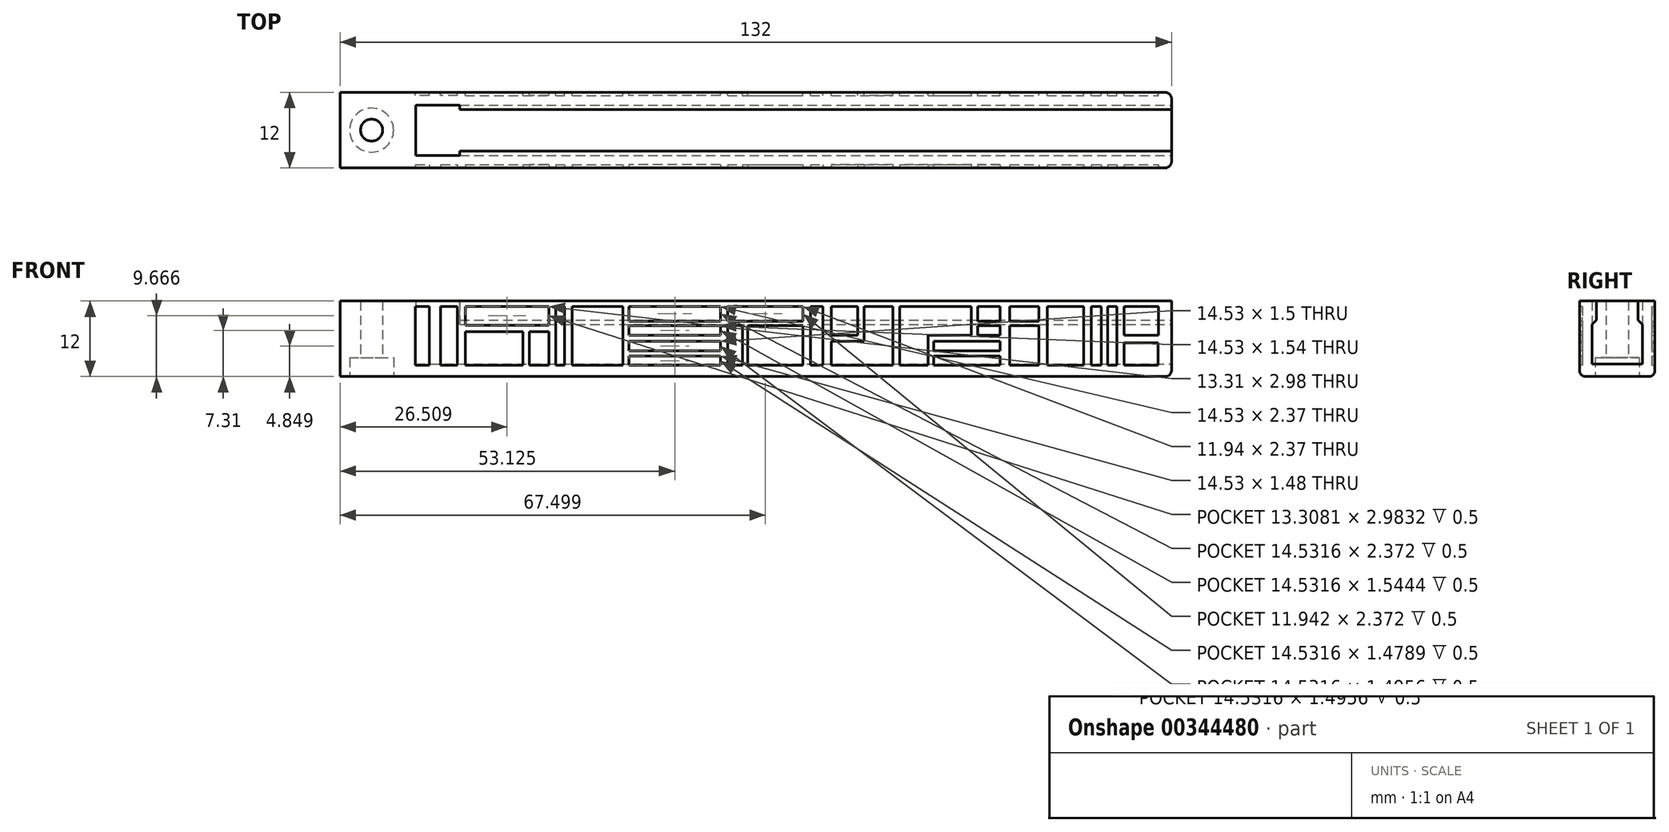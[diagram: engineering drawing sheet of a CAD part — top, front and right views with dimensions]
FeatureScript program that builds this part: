
annotation { "Feature Type Name" : "Feature", "Feature Type Description" : "" }
export const myFeature = defineFeature(function(context is Context, id is Id, definition is map)
    precondition{}
    {
        {
            var Q0;
            Q0=qCreatedBy(makeId("Top.planeOp"),FACE);
            var sketch = newSketch(context, id + "F0", { "sketchPlane" : qUnion([Q0])});
            skLineSegment(sketch, "E0.bottom", {"start": v(0, 0) * mm, "end": v(132, 0) * mm});
            skLineSegment(sketch, "E0.top", {"start": v(0, 12) * mm, "end": v(132, 12) * mm});
            skLineSegment(sketch, "E0.left", {"start": v(0, 0) * mm, "end": v(0, 12) * mm});
            skLineSegment(sketch, "E0.right", {"start": v(132, 0) * mm, "end": v(132, 12) * mm});
            skSolve(sketch);
        }
        {
            var Q0;
            Q0 = qSketchRegion(id + "F0", true);
            extrude(context, id + "F1", {"entities" : qUnion([Q0]), "depth" : 12 * mm, "offsetDistance" : 25 * mm});
        }
        {
            var Q0;
            Q0=makeQuery(id+"F1.opExtrude","SWEPT_FACE",FACE,{"disambiguationData":[OSD([sQuery(id+"F0.wireOp",EDGE,"E0.right")])]});
            var sketch = newSketch(context, id + "F2", { "sketchPlane" : qUnion([Q0])});
            skLineSegment(sketch, "E1.MirrorCS", {"start": v(2.7, 12) * mm, "end": v(2.7, 9) * mm});
            skLineSegment(sketch, "E2.MirrorCS", {"start": v(2.7, 9) * mm, "end": v(2, 8.3) * mm});
            skLineSegment(sketch, "E3.MirrorCS", {"start": v(2, 8.3) * mm, "end": v(2, 2) * mm});
            skLineSegment(sketch, "E4.MirrorCS", {"start": v(2, 2) * mm, "end": v(6, 2) * mm});
            skLineSegment(sketch, "E5", {"start": v(6, 2) * mm, "end": v(6, 12.64) * mm, "construction": true});
            skLineSegment(sketch, "E6.MirrorCS", {"start": v(9.3, 12) * mm, "end": v(9.3, 9) * mm});
            skLineSegment(sketch, "E7.MirrorCS", {"start": v(9.3, 9) * mm, "end": v(10, 8.3) * mm});
            skLineSegment(sketch, "E8.MirrorCS", {"start": v(10, 8.3) * mm, "end": v(10, 2) * mm});
            skLineSegment(sketch, "E9.MirrorCS", {"start": v(10, 2) * mm, "end": v(6, 2) * mm});
            skSolve(sketch);
        }
        {
            var Q0;
            {var subQ0=sQuery(id+"F2.wireOp",EDGE,"E1.MirrorCS");Q0=makeQuery(id+"F2.imprint","IMPRINT",FACE,{"disambiguationData":[TD([[makeQuery(id+"F2.imprint","IMPRINT",EDGE,{"derivedFrom":subQ0}),1.0]])]});}
            extrude(context, id + "F3", {"entities" : qUnion([Q0]), "operationType" : NewBodyOperationType.REMOVE, "oppositeDirection" : true, "depth" : 120 * mm, "offsetDistance" : 25 * mm});
        }
        {
            var Q0;
            Q0=makeQuery(id+"F1.opExtrude","CAP_EDGE",EDGE,{"disambiguationData":[OSD([sQuery(id+"F0.wireOp",EDGE,"E0.top")])],"isStart":true});
            var Q1;
            Q1=makeQuery(id+"F1.opExtrude","CAP_EDGE",EDGE,{"disambiguationData":[OSD([sQuery(id+"F0.wireOp",EDGE,"E0.bottom")])],"isStart":true});
            fillet(context, id + "F4", {"entities" : qUnion([Q0, Q1]), "radius" : 1 * mm, "tangentPropagation" : true, "allowEdgeOverflow" : false});
        }
        {
            var Q0;
            Q0=makeQuery(id+"F1.opExtrude","SWEPT_EDGE",EDGE,{"disambiguationData":[OSD([sQuery(id+"F0.wireOp",EDGE,"E0.top"),sQuery(id+"F0.wireOp",EDGE,"E0.right")])]});
            fillet(context, id + "F5", {"entities" : qUnion([Q0]), "radius" : 1 * mm, "tangentPropagation" : true, "allowEdgeOverflow" : false});
        }
        {
            var Q0;
            Q0=makeQuery(id+"F1.opExtrude","CAP_FACE",FACE,{"disambiguationData":[OSD([sQuery(id+"F0.wireOp",EDGE,"E0.bottom"),sQuery(id+"F0.wireOp",EDGE,"E0.top"),sQuery(id+"F0.wireOp",EDGE,"E0.left"),sQuery(id+"F0.wireOp",EDGE,"E0.right")])],"isStart":true});
            var sketch = newSketch(context, id + "F6", { "sketchPlane" : qUnion([Q0])});
            skCircle(sketch, "E10", {"center": v(5, -6) * mm, "radius": 1.75 * mm});
            skPoint(sketch, "E10.centerSnap0", {"position": v(0, -6) * mm});
            skSolve(sketch);
        }
        {
            var Q0;
            Q0 = qSketchRegion(id + "F6", true);
            extrude(context, id + "F7", {"entities" : qUnion([Q0]), "operationType" : NewBodyOperationType.REMOVE, "oppositeDirection" : true, "depth" : 25 * mm, "offsetDistance" : 25 * mm});
        }
        {
            var Q0;
            Q0=makeQuery(id+"F1.opExtrude","CAP_FACE",FACE,{"disambiguationData":[OSD([sQuery(id+"F0.wireOp",EDGE,"E0.bottom"),sQuery(id+"F0.wireOp",EDGE,"E0.top"),sQuery(id+"F0.wireOp",EDGE,"E0.left"),sQuery(id+"F0.wireOp",EDGE,"E0.right")])],"isStart":true});
            var sketch = newSketch(context, id + "F8", { "sketchPlane" : qUnion([Q0])});
            skCircle(sketch, "E11", {"center": v(5, -6) * mm, "radius": 3.5 * mm});
            skSolve(sketch);
        }
        {
            var Q0;
            Q0 = qSketchRegion(id + "F8", true);
            extrude(context, id + "F9", {"entities" : qUnion([Q0]), "operationType" : NewBodyOperationType.REMOVE, "oppositeDirection" : true, "depth" : 3 * mm, "offsetDistance" : 25 * mm});
        }
        {
            var Q0;
            Q0=makeQuery(id+"F3.boolean.opBoolean","COPY",FACE,{"derivedFrom":makeQuery(id+"F3.opExtrude","SWEPT_FACE",FACE,{"disambiguationData":[OSD([sQuery(id+"F2.wireOp",EDGE,"E4.MirrorCS"),sQuery(id+"F2.wireOp",EDGE,"E9.MirrorCS")])]})});
            var sketch = newSketch(context, id + "F10", { "sketchPlane" : qUnion([Q0])});
            skLineSegment(sketch, "E12.bottom", {"start": v(12, 10) * mm, "end": v(19, 10) * mm});
            skLineSegment(sketch, "E12.top", {"start": v(12, 2) * mm, "end": v(19, 2) * mm});
            skLineSegment(sketch, "E12.left", {"start": v(12, 10) * mm, "end": v(12, 2) * mm});
            skLineSegment(sketch, "E12.right", {"start": v(19, 10) * mm, "end": v(19, 2) * mm});
            skSolve(sketch);
        }
        {
            var Q0;
            Q0 = qSketchRegion(id + "F10", true);
            extrude(context, id + "F11", {"entities" : qUnion([Q0]), "operationType" : NewBodyOperationType.REMOVE, "depth" : 25 * mm, "offsetDistance" : 25 * mm});
        }
        {
            var Q0;
            Q0=makeQuery(id+"F1.opExtrude","SWEPT_FACE",FACE,{"disambiguationData":[OSD([sQuery(id+"F0.wireOp",EDGE,"E0.top")])]});
            var sketch = newSketch(context, id + "F12", { "sketchPlane" : qUnion([Q0])});
            skLineSegment(sketch, "E13.bottom", {"start": v(-19.85, 1.79) * mm, "end": v(-19.85, 7.11) * mm});
            skLineSegment(sketch, "E13.top", {"start": v(-29.03, 1.79) * mm, "end": v(-29.03, 7.11) * mm});
            skLineSegment(sketch, "E13.left", {"start": v(-19.85, 1.79) * mm, "end": v(-29.03, 1.79) * mm});
            skLineSegment(sketch, "E13.right", {"start": v(-19.85, 7.11) * mm, "end": v(-29.03, 7.11) * mm});
            skLineSegment(sketch, "E14.bottom", {"start": v(-19.85, 8.17) * mm, "end": v(-19.85, 11.16) * mm});
            skLineSegment(sketch, "E14.top", {"start": v(-33.16, 8.17) * mm, "end": v(-33.16, 11.16) * mm});
            skLineSegment(sketch, "E14.left", {"start": v(-19.85, 8.17) * mm, "end": v(-33.16, 8.17) * mm});
            skLineSegment(sketch, "E14.right", {"start": v(-19.85, 11.16) * mm, "end": v(-33.16, 11.16) * mm});
            skPoint(sketch, "E15.firstSnap0", {"position": v(-33.16, 9.67) * mm});
            skLineSegment(sketch, "E15.bottom", {"start": v(-33.16, 1.79) * mm, "end": v(-33.16, 7.11) * mm});
            skLineSegment(sketch, "E15.top", {"start": v(-30.04, 1.79) * mm, "end": v(-30.04, 7.11) * mm});
            skLineSegment(sketch, "E15.left", {"start": v(-33.16, 1.79) * mm, "end": v(-30.04, 1.79) * mm});
            skLineSegment(sketch, "E15.right", {"start": v(-33.16, 7.11) * mm, "end": v(-30.04, 7.11) * mm});
            skLineSegment(sketch, "E16.bottom", {"start": v(-34.2, 1.79) * mm, "end": v(-34.2, 11.16) * mm});
            skLineSegment(sketch, "E16.top", {"start": v(-35.66, 1.79) * mm, "end": v(-35.66, 11.16) * mm});
            skLineSegment(sketch, "E16.left", {"start": v(-34.2, 1.79) * mm, "end": v(-35.66, 1.79) * mm});
            skLineSegment(sketch, "E16.right", {"start": v(-34.2, 11.16) * mm, "end": v(-35.66, 11.16) * mm});
            skLineSegment(sketch, "E17.bottom", {"start": v(-36.83, 1.79) * mm, "end": v(-36.83, 11.16) * mm});
            skLineSegment(sketch, "E17.top", {"start": v(-44.9, 1.79) * mm, "end": v(-44.9, 11.16) * mm});
            skLineSegment(sketch, "E17.left", {"start": v(-36.83, 1.79) * mm, "end": v(-44.9, 1.79) * mm});
            skLineSegment(sketch, "E17.right", {"start": v(-36.83, 11.16) * mm, "end": v(-44.9, 11.16) * mm});
            skLineSegment(sketch, "E18.bottom", {"start": v(-45.86, 1.79) * mm, "end": v(-45.86, 3.27) * mm});
            skLineSegment(sketch, "E18.top", {"start": v(-60.4, 1.79) * mm, "end": v(-60.4, 3.27) * mm});
            skLineSegment(sketch, "E18.left", {"start": v(-45.86, 1.79) * mm, "end": v(-60.4, 1.79) * mm});
            skLineSegment(sketch, "E18.right", {"start": v(-45.86, 3.27) * mm, "end": v(-60.4, 3.27) * mm});
            skLineSegment(sketch, "E19.bottom", {"start": v(-60.4, 4.1) * mm, "end": v(-60.4, 5.6) * mm});
            skLineSegment(sketch, "E19.top", {"start": v(-45.86, 4.1) * mm, "end": v(-45.86, 5.6) * mm});
            skLineSegment(sketch, "E19.left", {"start": v(-60.4, 4.1) * mm, "end": v(-45.86, 4.1) * mm});
            skLineSegment(sketch, "E19.right", {"start": v(-60.4, 5.6) * mm, "end": v(-45.86, 5.6) * mm});
            skLineSegment(sketch, "E20.bottom", {"start": v(-45.86, 6.54) * mm, "end": v(-45.86, 8.08) * mm});
            skLineSegment(sketch, "E20.top", {"start": v(-60.4, 6.54) * mm, "end": v(-60.4, 8.08) * mm});
            skLineSegment(sketch, "E20.left", {"start": v(-45.86, 6.54) * mm, "end": v(-60.4, 6.54) * mm});
            skLineSegment(sketch, "E20.right", {"start": v(-45.86, 8.08) * mm, "end": v(-60.4, 8.08) * mm});
            skLineSegment(sketch, "E21.bottom", {"start": v(-60.4, 8.79) * mm, "end": v(-60.4, 11.16) * mm});
            skLineSegment(sketch, "E21.top", {"start": v(-45.86, 8.79) * mm, "end": v(-45.86, 11.16) * mm});
            skLineSegment(sketch, "E21.left", {"start": v(-60.4, 8.79) * mm, "end": v(-45.86, 8.79) * mm});
            skLineSegment(sketch, "E21.right", {"start": v(-60.4, 11.16) * mm, "end": v(-45.86, 11.16) * mm});
            skLineSegment(sketch, "E22.bottom", {"start": v(-61.53, 1.79) * mm, "end": v(-61.53, 8.08) * mm});
            skLineSegment(sketch, "E22.top", {"start": v(-63.86, 1.79) * mm, "end": v(-63.86, 8.08) * mm});
            skLineSegment(sketch, "E22.left", {"start": v(-61.53, 1.79) * mm, "end": v(-63.86, 1.79) * mm});
            skLineSegment(sketch, "E22.right", {"start": v(-61.53, 8.08) * mm, "end": v(-63.86, 8.08) * mm});
            skLineSegment(sketch, "E23.bottom", {"start": v(-61.53, 8.79) * mm, "end": v(-61.53, 11.16) * mm});
            skLineSegment(sketch, "E23.top", {"start": v(-73.47, 8.79) * mm, "end": v(-73.47, 11.16) * mm});
            skLineSegment(sketch, "E23.left", {"start": v(-61.53, 8.79) * mm, "end": v(-73.47, 8.79) * mm});
            skLineSegment(sketch, "E23.right", {"start": v(-61.53, 11.16) * mm, "end": v(-73.47, 11.16) * mm});
            skLineSegment(sketch, "E24.bottom", {"start": v(-64.7, 1.79) * mm, "end": v(-64.7, 8.08) * mm});
            skLineSegment(sketch, "E24.top", {"start": v(-73.47, 1.79) * mm, "end": v(-73.47, 8.08) * mm});
            skLineSegment(sketch, "E24.left", {"start": v(-64.7, 1.79) * mm, "end": v(-73.47, 1.79) * mm});
            skLineSegment(sketch, "E24.right", {"start": v(-64.7, 8.08) * mm, "end": v(-73.47, 8.08) * mm});
            skLineSegment(sketch, "E25.bottom", {"start": v(-74.65, 11.16) * mm, "end": v(-74.65, 1.79) * mm});
            skLineSegment(sketch, "E25.top", {"start": v(-76.62, 11.16) * mm, "end": v(-76.62, 1.79) * mm});
            skLineSegment(sketch, "E25.left", {"start": v(-74.65, 11.16) * mm, "end": v(-76.62, 11.16) * mm});
            skLineSegment(sketch, "E25.right", {"start": v(-74.65, 1.79) * mm, "end": v(-76.62, 1.79) * mm});
            skLineSegment(sketch, "E26.bottom", {"start": v(-77.98, 11.16) * mm, "end": v(-77.98, 6.54) * mm});
            skLineSegment(sketch, "E26.top", {"start": v(-82.17, 11.16) * mm, "end": v(-82.17, 6.54) * mm});
            skLineSegment(sketch, "E26.left", {"start": v(-77.98, 11.16) * mm, "end": v(-82.17, 11.16) * mm});
            skLineSegment(sketch, "E26.right", {"start": v(-77.98, 6.54) * mm, "end": v(-82.17, 6.54) * mm});
            skLineSegment(sketch, "E27.bottom", {"start": v(-77.98, 5.6) * mm, "end": v(-77.98, 1.79) * mm});
            skLineSegment(sketch, "E27.top", {"start": v(-87.79, 5.6) * mm, "end": v(-87.79, 1.79) * mm});
            skLineSegment(sketch, "E27.left", {"start": v(-77.98, 5.6) * mm, "end": v(-87.79, 5.6) * mm});
            skLineSegment(sketch, "E27.right", {"start": v(-77.98, 1.79) * mm, "end": v(-87.79, 1.79) * mm});
            skLineSegment(sketch, "E28.bottom", {"start": v(-87.79, 5.6) * mm, "end": v(-87.79, 11.16) * mm});
            skLineSegment(sketch, "E28.top", {"start": v(-83.2, 5.6) * mm, "end": v(-83.2, 11.16) * mm});
            skLineSegment(sketch, "E28.left", {"start": v(-87.79, 5.6) * mm, "end": v(-83.2, 5.6) * mm});
            skLineSegment(sketch, "E28.right", {"start": v(-87.79, 11.16) * mm, "end": v(-83.2, 11.16) * mm});
            skLineSegment(sketch, "E29.bottom", {"start": v(-88.87, 1.79) * mm, "end": v(-88.87, 11.16) * mm});
            skLineSegment(sketch, "E29.top", {"start": v(-93.38, 1.79) * mm, "end": v(-93.38, 11.16) * mm});
            skLineSegment(sketch, "E29.left", {"start": v(-88.87, 1.79) * mm, "end": v(-93.38, 1.79) * mm});
            skLineSegment(sketch, "E29.right", {"start": v(-88.87, 11.16) * mm, "end": v(-93.38, 11.16) * mm});
            skLineSegment(sketch, "E30.bottom", {"start": v(-93.38, 11.16) * mm, "end": v(-93.38, 6.54) * mm});
            skLineSegment(sketch, "E30.top", {"start": v(-100.19, 11.16) * mm, "end": v(-100.19, 6.54) * mm});
            skLineSegment(sketch, "E30.left", {"start": v(-93.38, 11.16) * mm, "end": v(-100.19, 11.16) * mm});
            skLineSegment(sketch, "E30.right", {"start": v(-93.38, 6.54) * mm, "end": v(-100.19, 6.54) * mm});
            skLineSegment(sketch, "E31.bottom", {"start": v(-94.25, 1.79) * mm, "end": v(-94.25, 3.27) * mm});
            skLineSegment(sketch, "E31.top", {"start": v(-104.75, 1.79) * mm, "end": v(-104.75, 3.27) * mm});
            skLineSegment(sketch, "E31.left", {"start": v(-94.25, 1.79) * mm, "end": v(-104.75, 1.79) * mm});
            skLineSegment(sketch, "E31.right", {"start": v(-94.25, 3.27) * mm, "end": v(-104.75, 3.27) * mm});
            skLineSegment(sketch, "E32.bottom", {"start": v(-94.25, 4.1) * mm, "end": v(-94.25, 5.6) * mm});
            skLineSegment(sketch, "E32.top", {"start": v(-104.75, 4.1) * mm, "end": v(-104.75, 5.6) * mm});
            skLineSegment(sketch, "E32.left", {"start": v(-94.25, 4.1) * mm, "end": v(-104.75, 4.1) * mm});
            skLineSegment(sketch, "E32.right", {"start": v(-94.25, 5.6) * mm, "end": v(-104.75, 5.6) * mm});
            skLineSegment(sketch, "E33.bottom", {"start": v(-104.75, 6.54) * mm, "end": v(-104.75, 8.08) * mm});
            skLineSegment(sketch, "E33.top", {"start": v(-101.21, 6.54) * mm, "end": v(-101.21, 8.08) * mm});
            skLineSegment(sketch, "E33.left", {"start": v(-104.75, 6.54) * mm, "end": v(-101.21, 6.54) * mm});
            skLineSegment(sketch, "E33.right", {"start": v(-104.75, 8.08) * mm, "end": v(-101.21, 8.08) * mm});
            skLineSegment(sketch, "E34.bottom", {"start": v(-101.21, 8.79) * mm, "end": v(-101.21, 11.16) * mm});
            skLineSegment(sketch, "E34.top", {"start": v(-104.75, 8.79) * mm, "end": v(-104.75, 11.16) * mm});
            skLineSegment(sketch, "E34.left", {"start": v(-101.21, 8.79) * mm, "end": v(-104.75, 8.79) * mm});
            skLineSegment(sketch, "E34.right", {"start": v(-101.21, 11.16) * mm, "end": v(-104.75, 11.16) * mm});
            skLineSegment(sketch, "E35.bottom", {"start": v(-106.32, 1.79) * mm, "end": v(-106.32, 8.08) * mm});
            skLineSegment(sketch, "E35.top", {"start": v(-110.94, 1.79) * mm, "end": v(-110.94, 8.08) * mm});
            skLineSegment(sketch, "E35.left", {"start": v(-106.32, 1.79) * mm, "end": v(-110.94, 1.79) * mm});
            skLineSegment(sketch, "E35.right", {"start": v(-106.32, 8.08) * mm, "end": v(-110.94, 8.08) * mm});
            skLineSegment(sketch, "E36.bottom", {"start": v(-112.25, 1.79) * mm, "end": v(-112.25, 11.16) * mm});
            skLineSegment(sketch, "E36.top", {"start": v(-118.04, 1.79) * mm, "end": v(-118.04, 11.16) * mm});
            skLineSegment(sketch, "E36.left", {"start": v(-112.25, 1.79) * mm, "end": v(-118.04, 1.79) * mm});
            skLineSegment(sketch, "E36.right", {"start": v(-112.25, 11.16) * mm, "end": v(-118.04, 11.16) * mm});
            skLineSegment(sketch, "E37.bottom", {"start": v(-106.32, 8.79) * mm, "end": v(-106.32, 11.16) * mm});
            skLineSegment(sketch, "E37.top", {"start": v(-110.94, 8.79) * mm, "end": v(-110.94, 11.16) * mm});
            skLineSegment(sketch, "E37.left", {"start": v(-106.32, 8.79) * mm, "end": v(-110.94, 8.79) * mm});
            skLineSegment(sketch, "E37.right", {"start": v(-106.32, 11.16) * mm, "end": v(-110.94, 11.16) * mm});
            skLineSegment(sketch, "E38.bottom", {"start": v(-119.28, 1.79) * mm, "end": v(-119.28, 11.16) * mm});
            skLineSegment(sketch, "E38.top", {"start": v(-120.87, 1.79) * mm, "end": v(-120.87, 11.16) * mm});
            skLineSegment(sketch, "E38.left", {"start": v(-119.28, 1.79) * mm, "end": v(-120.87, 1.79) * mm});
            skLineSegment(sketch, "E38.right", {"start": v(-119.28, 11.16) * mm, "end": v(-120.87, 11.16) * mm});
            skLineSegment(sketch, "E39.bottom", {"start": v(-121.84, 1.79) * mm, "end": v(-121.84, 11.16) * mm});
            skLineSegment(sketch, "E39.top", {"start": v(-123.3, 1.79) * mm, "end": v(-123.3, 11.16) * mm});
            skLineSegment(sketch, "E39.left", {"start": v(-121.84, 1.79) * mm, "end": v(-123.3, 1.79) * mm});
            skLineSegment(sketch, "E39.right", {"start": v(-121.84, 11.16) * mm, "end": v(-123.3, 11.16) * mm});
            skLineSegment(sketch, "E40.bottom", {"start": v(-124.5, 6.54) * mm, "end": v(-124.5, 11.16) * mm});
            skLineSegment(sketch, "E40.top", {"start": v(-129.93, 6.54) * mm, "end": v(-129.93, 11.16) * mm});
            skLineSegment(sketch, "E40.left", {"start": v(-124.5, 6.54) * mm, "end": v(-129.93, 6.54) * mm});
            skLineSegment(sketch, "E40.right", {"start": v(-124.5, 11.16) * mm, "end": v(-129.93, 11.16) * mm});
            skLineSegment(sketch, "E41.bottom", {"start": v(-124.5, 5.33) * mm, "end": v(-124.5, 1.79) * mm});
            skLineSegment(sketch, "E41.top", {"start": v(-129.85, 5.33) * mm, "end": v(-129.85, 1.79) * mm});
            skLineSegment(sketch, "E41.left", {"start": v(-124.5, 5.33) * mm, "end": v(-129.85, 5.33) * mm});
            skLineSegment(sketch, "E41.right", {"start": v(-124.5, 1.79) * mm, "end": v(-129.85, 1.79) * mm});
            skLineSegment(sketch, "E42.bottom", {"start": v(-18.63, 11.16) * mm, "end": v(-15.96, 11.16) * mm});
            skLineSegment(sketch, "E42.top", {"start": v(-18.63, 1.79) * mm, "end": v(-15.96, 1.79) * mm});
            skLineSegment(sketch, "E42.left", {"start": v(-18.63, 11.16) * mm, "end": v(-18.63, 1.79) * mm});
            skLineSegment(sketch, "E42.right", {"start": v(-15.96, 11.16) * mm, "end": v(-15.96, 1.79) * mm});
            skLineSegment(sketch, "E43.bottom", {"start": v(-14.16, 1.79) * mm, "end": v(-11.96, 1.79) * mm});
            skLineSegment(sketch, "E43.top", {"start": v(-14.16, 11.16) * mm, "end": v(-11.96, 11.16) * mm});
            skLineSegment(sketch, "E43.left", {"start": v(-14.16, 1.79) * mm, "end": v(-14.16, 11.16) * mm});
            skLineSegment(sketch, "E43.right", {"start": v(-11.96, 1.79) * mm, "end": v(-11.96, 11.16) * mm});
            skSolve(sketch);
        }
        {
            var Q0;
            Q0 = qSketchRegion(id + "F12", true);
            extrude(context, id + "F13", {"entities" : qUnion([Q0]), "operationType" : NewBodyOperationType.REMOVE, "oppositeDirection" : true, "depth" : 0.5 * mm, "offsetDistance" : 25 * mm});
        }
        {
            var Q0;
            Q0=makeQuery(id+"F1.opExtrude","SWEPT_FACE",FACE,{"disambiguationData":[OSD([sQuery(id+"F0.wireOp",EDGE,"E0.bottom")])]});
            var sketch = newSketch(context, id + "F14", { "sketchPlane" : qUnion([Q0])});
            skLineSegment(sketch, "E44.0.0", {"start": v(11.96, 11.16) * mm, "end": v(14.16, 11.16) * mm});
            skLineSegment(sketch, "E44.0.1", {"start": v(14.16, 11.16) * mm, "end": v(14.16, 1.79) * mm});
            skLineSegment(sketch, "E44.0.2", {"start": v(14.16, 1.79) * mm, "end": v(11.96, 1.79) * mm});
            skLineSegment(sketch, "E44.0.3", {"start": v(11.96, 1.79) * mm, "end": v(11.96, 11.16) * mm});
            skLineSegment(sketch, "E44.1.0", {"start": v(18.63, 11.16) * mm, "end": v(18.63, 1.79) * mm});
            skLineSegment(sketch, "E44.1.1", {"start": v(18.63, 1.79) * mm, "end": v(15.96, 1.79) * mm});
            skLineSegment(sketch, "E44.1.2", {"start": v(15.96, 1.79) * mm, "end": v(15.96, 11.16) * mm});
            skLineSegment(sketch, "E44.1.3", {"start": v(15.96, 11.16) * mm, "end": v(18.63, 11.16) * mm});
            skLineSegment(sketch, "E44.2.0", {"start": v(33.16, 11.16) * mm, "end": v(33.16, 8.17) * mm});
            skLineSegment(sketch, "E44.2.1", {"start": v(33.16, 8.17) * mm, "end": v(19.85, 8.17) * mm});
            skLineSegment(sketch, "E44.2.2", {"start": v(19.85, 8.17) * mm, "end": v(19.85, 11.16) * mm});
            skLineSegment(sketch, "E44.2.3", {"start": v(19.85, 11.16) * mm, "end": v(33.16, 11.16) * mm});
            skLineSegment(sketch, "E44.3.0", {"start": v(29.03, 7.11) * mm, "end": v(29.03, 1.79) * mm});
            skLineSegment(sketch, "E44.3.1", {"start": v(29.03, 1.79) * mm, "end": v(19.85, 1.79) * mm});
            skLineSegment(sketch, "E44.3.2", {"start": v(19.85, 1.79) * mm, "end": v(19.85, 7.11) * mm});
            skLineSegment(sketch, "E44.3.3", {"start": v(19.85, 7.11) * mm, "end": v(29.03, 7.11) * mm});
            skLineSegment(sketch, "E44.4.0", {"start": v(33.16, 1.79) * mm, "end": v(30.04, 1.79) * mm});
            skLineSegment(sketch, "E44.4.1", {"start": v(30.04, 1.79) * mm, "end": v(30.04, 7.11) * mm});
            skLineSegment(sketch, "E44.4.2", {"start": v(30.04, 7.11) * mm, "end": v(33.16, 7.11) * mm});
            skLineSegment(sketch, "E44.4.3", {"start": v(33.16, 7.11) * mm, "end": v(33.16, 1.79) * mm});
            skLineSegment(sketch, "E44.5.0", {"start": v(35.66, 11.16) * mm, "end": v(35.66, 1.79) * mm});
            skLineSegment(sketch, "E44.5.1", {"start": v(35.66, 1.79) * mm, "end": v(34.2, 1.79) * mm});
            skLineSegment(sketch, "E44.5.2", {"start": v(34.2, 1.79) * mm, "end": v(34.2, 11.16) * mm});
            skLineSegment(sketch, "E44.5.3", {"start": v(34.2, 11.16) * mm, "end": v(35.66, 11.16) * mm});
            skLineSegment(sketch, "E44.6.0", {"start": v(44.9, 11.16) * mm, "end": v(44.9, 1.79) * mm});
            skLineSegment(sketch, "E44.6.1", {"start": v(44.9, 1.79) * mm, "end": v(36.83, 1.79) * mm});
            skLineSegment(sketch, "E44.6.2", {"start": v(36.83, 1.79) * mm, "end": v(36.83, 11.16) * mm});
            skLineSegment(sketch, "E44.6.3", {"start": v(36.83, 11.16) * mm, "end": v(44.9, 11.16) * mm});
            skLineSegment(sketch, "E44.7.0", {"start": v(60.4, 8.79) * mm, "end": v(45.86, 8.79) * mm});
            skLineSegment(sketch, "E44.7.1", {"start": v(45.86, 8.79) * mm, "end": v(45.86, 11.16) * mm});
            skLineSegment(sketch, "E44.7.2", {"start": v(45.86, 11.16) * mm, "end": v(60.4, 11.16) * mm});
            skLineSegment(sketch, "E44.7.3", {"start": v(60.4, 11.16) * mm, "end": v(60.4, 8.79) * mm});
            skLineSegment(sketch, "E44.8.0", {"start": v(60.4, 8.08) * mm, "end": v(60.4, 6.54) * mm});
            skLineSegment(sketch, "E44.8.1", {"start": v(60.4, 6.54) * mm, "end": v(45.86, 6.54) * mm});
            skLineSegment(sketch, "E44.8.2", {"start": v(45.86, 6.54) * mm, "end": v(45.86, 8.08) * mm});
            skLineSegment(sketch, "E44.8.3", {"start": v(45.86, 8.08) * mm, "end": v(60.4, 8.08) * mm});
            skLineSegment(sketch, "E44.9.0", {"start": v(60.4, 4.1) * mm, "end": v(45.86, 4.1) * mm});
            skLineSegment(sketch, "E44.9.1", {"start": v(45.86, 4.1) * mm, "end": v(45.86, 5.6) * mm});
            skLineSegment(sketch, "E44.9.2", {"start": v(45.86, 5.6) * mm, "end": v(60.4, 5.6) * mm});
            skLineSegment(sketch, "E44.9.3", {"start": v(60.4, 5.6) * mm, "end": v(60.4, 4.1) * mm});
            skLineSegment(sketch, "E44.10.0", {"start": v(60.4, 3.27) * mm, "end": v(60.4, 1.79) * mm});
            skLineSegment(sketch, "E44.10.1", {"start": v(60.4, 1.79) * mm, "end": v(45.86, 1.79) * mm});
            skLineSegment(sketch, "E44.10.2", {"start": v(45.86, 1.79) * mm, "end": v(45.86, 3.27) * mm});
            skLineSegment(sketch, "E44.10.3", {"start": v(45.86, 3.27) * mm, "end": v(60.4, 3.27) * mm});
            skLineSegment(sketch, "E44.11.0", {"start": v(63.86, 8.08) * mm, "end": v(63.86, 1.79) * mm});
            skLineSegment(sketch, "E44.11.1", {"start": v(63.86, 1.79) * mm, "end": v(61.53, 1.79) * mm});
            skLineSegment(sketch, "E44.11.2", {"start": v(61.53, 1.79) * mm, "end": v(61.53, 8.08) * mm});
            skLineSegment(sketch, "E44.11.3", {"start": v(61.53, 8.08) * mm, "end": v(63.86, 8.08) * mm});
            skLineSegment(sketch, "E44.12.0", {"start": v(73.47, 11.16) * mm, "end": v(73.47, 8.79) * mm});
            skLineSegment(sketch, "E44.12.1", {"start": v(73.47, 8.79) * mm, "end": v(61.53, 8.79) * mm});
            skLineSegment(sketch, "E44.12.2", {"start": v(61.53, 8.79) * mm, "end": v(61.53, 11.16) * mm});
            skLineSegment(sketch, "E44.12.3", {"start": v(61.53, 11.16) * mm, "end": v(73.47, 11.16) * mm});
            skLineSegment(sketch, "E44.13.0", {"start": v(73.47, 8.08) * mm, "end": v(73.47, 1.79) * mm});
            skLineSegment(sketch, "E44.13.1", {"start": v(73.47, 1.79) * mm, "end": v(64.7, 1.79) * mm});
            skLineSegment(sketch, "E44.13.2", {"start": v(64.7, 1.79) * mm, "end": v(64.7, 8.08) * mm});
            skLineSegment(sketch, "E44.13.3", {"start": v(64.7, 8.08) * mm, "end": v(73.47, 8.08) * mm});
            skLineSegment(sketch, "E44.14.0", {"start": v(74.65, 11.16) * mm, "end": v(76.62, 11.16) * mm});
            skLineSegment(sketch, "E44.14.1", {"start": v(76.62, 11.16) * mm, "end": v(76.62, 1.79) * mm});
            skLineSegment(sketch, "E44.14.2", {"start": v(76.62, 1.79) * mm, "end": v(74.65, 1.79) * mm});
            skLineSegment(sketch, "E44.14.3", {"start": v(74.65, 1.79) * mm, "end": v(74.65, 11.16) * mm});
            skLineSegment(sketch, "E44.15.0", {"start": v(77.98, 11.16) * mm, "end": v(82.17, 11.16) * mm});
            skLineSegment(sketch, "E44.15.1", {"start": v(82.17, 11.16) * mm, "end": v(82.17, 6.54) * mm});
            skLineSegment(sketch, "E44.15.2", {"start": v(82.17, 6.54) * mm, "end": v(77.98, 6.54) * mm});
            skLineSegment(sketch, "E44.15.3", {"start": v(77.98, 6.54) * mm, "end": v(77.98, 11.16) * mm});
            skLineSegment(sketch, "E44.16.0", {"start": v(77.98, 5.6) * mm, "end": v(83.2, 5.6) * mm});
            skLineSegment(sketch, "E44.16.1", {"start": v(83.2, 5.6) * mm, "end": v(83.2, 11.16) * mm});
            skLineSegment(sketch, "E44.16.2", {"start": v(83.2, 11.16) * mm, "end": v(87.79, 11.16) * mm});
            skLineSegment(sketch, "E44.16.3", {"start": v(87.79, 11.16) * mm, "end": v(87.79, 1.79) * mm});
            skLineSegment(sketch, "E44.16.4", {"start": v(87.79, 1.79) * mm, "end": v(77.98, 1.79) * mm});
            skLineSegment(sketch, "E44.16.5", {"start": v(77.98, 1.79) * mm, "end": v(77.98, 5.6) * mm});
            skLineSegment(sketch, "E44.17.0", {"start": v(93.38, 6.54) * mm, "end": v(93.38, 1.79) * mm});
            skLineSegment(sketch, "E44.17.1", {"start": v(93.38, 1.79) * mm, "end": v(88.87, 1.79) * mm});
            skLineSegment(sketch, "E44.17.2", {"start": v(88.87, 1.79) * mm, "end": v(88.87, 11.16) * mm});
            skLineSegment(sketch, "E44.17.3", {"start": v(88.87, 11.16) * mm, "end": v(100.19, 11.16) * mm});
            skLineSegment(sketch, "E44.17.4", {"start": v(100.19, 11.16) * mm, "end": v(100.19, 6.54) * mm});
            skLineSegment(sketch, "E44.17.5", {"start": v(100.19, 6.54) * mm, "end": v(93.38, 6.54) * mm});
            skLineSegment(sketch, "E44.18.0", {"start": v(104.75, 11.16) * mm, "end": v(104.75, 8.79) * mm});
            skLineSegment(sketch, "E44.18.1", {"start": v(104.75, 8.79) * mm, "end": v(101.21, 8.79) * mm});
            skLineSegment(sketch, "E44.18.2", {"start": v(101.21, 8.79) * mm, "end": v(101.21, 11.16) * mm});
            skLineSegment(sketch, "E44.18.3", {"start": v(101.21, 11.16) * mm, "end": v(104.75, 11.16) * mm});
            skLineSegment(sketch, "E44.19.0", {"start": v(104.75, 6.54) * mm, "end": v(101.21, 6.54) * mm});
            skLineSegment(sketch, "E44.19.1", {"start": v(101.21, 6.54) * mm, "end": v(101.21, 8.08) * mm});
            skLineSegment(sketch, "E44.19.2", {"start": v(101.21, 8.08) * mm, "end": v(104.75, 8.08) * mm});
            skLineSegment(sketch, "E44.19.3", {"start": v(104.75, 8.08) * mm, "end": v(104.75, 6.54) * mm});
            skLineSegment(sketch, "E44.20.0", {"start": v(104.75, 5.6) * mm, "end": v(104.75, 4.1) * mm});
            skLineSegment(sketch, "E44.20.1", {"start": v(104.75, 4.1) * mm, "end": v(94.25, 4.1) * mm});
            skLineSegment(sketch, "E44.20.2", {"start": v(94.25, 4.1) * mm, "end": v(94.25, 5.6) * mm});
            skLineSegment(sketch, "E44.20.3", {"start": v(94.25, 5.6) * mm, "end": v(104.75, 5.6) * mm});
            skLineSegment(sketch, "E44.21.0", {"start": v(104.75, 3.27) * mm, "end": v(104.75, 1.79) * mm});
            skLineSegment(sketch, "E44.21.1", {"start": v(104.75, 1.79) * mm, "end": v(94.25, 1.79) * mm});
            skLineSegment(sketch, "E44.21.2", {"start": v(94.25, 1.79) * mm, "end": v(94.25, 3.27) * mm});
            skLineSegment(sketch, "E44.21.3", {"start": v(94.25, 3.27) * mm, "end": v(104.75, 3.27) * mm});
            skLineSegment(sketch, "E44.22.0", {"start": v(110.94, 8.08) * mm, "end": v(110.94, 1.79) * mm});
            skLineSegment(sketch, "E44.22.1", {"start": v(110.94, 1.79) * mm, "end": v(106.32, 1.79) * mm});
            skLineSegment(sketch, "E44.22.2", {"start": v(106.32, 1.79) * mm, "end": v(106.32, 8.08) * mm});
            skLineSegment(sketch, "E44.22.3", {"start": v(106.32, 8.08) * mm, "end": v(110.94, 8.08) * mm});
            skLineSegment(sketch, "E44.23.0", {"start": v(110.94, 11.16) * mm, "end": v(110.94, 8.79) * mm});
            skLineSegment(sketch, "E44.23.1", {"start": v(110.94, 8.79) * mm, "end": v(106.32, 8.79) * mm});
            skLineSegment(sketch, "E44.23.2", {"start": v(106.32, 8.79) * mm, "end": v(106.32, 11.16) * mm});
            skLineSegment(sketch, "E44.23.3", {"start": v(106.32, 11.16) * mm, "end": v(110.94, 11.16) * mm});
            skLineSegment(sketch, "E44.24.0", {"start": v(118.04, 11.16) * mm, "end": v(118.04, 1.79) * mm});
            skLineSegment(sketch, "E44.24.1", {"start": v(118.04, 1.79) * mm, "end": v(112.25, 1.79) * mm});
            skLineSegment(sketch, "E44.24.2", {"start": v(112.25, 1.79) * mm, "end": v(112.25, 11.16) * mm});
            skLineSegment(sketch, "E44.24.3", {"start": v(112.25, 11.16) * mm, "end": v(118.04, 11.16) * mm});
            skLineSegment(sketch, "E44.25.0", {"start": v(120.87, 11.16) * mm, "end": v(120.87, 1.79) * mm});
            skLineSegment(sketch, "E44.25.1", {"start": v(120.87, 1.79) * mm, "end": v(119.28, 1.79) * mm});
            skLineSegment(sketch, "E44.25.2", {"start": v(119.28, 1.79) * mm, "end": v(119.28, 11.16) * mm});
            skLineSegment(sketch, "E44.25.3", {"start": v(119.28, 11.16) * mm, "end": v(120.87, 11.16) * mm});
            skLineSegment(sketch, "E44.26.0", {"start": v(123.3, 11.16) * mm, "end": v(123.3, 1.79) * mm});
            skLineSegment(sketch, "E44.26.1", {"start": v(123.3, 1.79) * mm, "end": v(121.84, 1.79) * mm});
            skLineSegment(sketch, "E44.26.2", {"start": v(121.84, 1.79) * mm, "end": v(121.84, 11.16) * mm});
            skLineSegment(sketch, "E44.26.3", {"start": v(121.84, 11.16) * mm, "end": v(123.3, 11.16) * mm});
            skLineSegment(sketch, "E44.27.0", {"start": v(129.93, 11.16) * mm, "end": v(129.93, 6.54) * mm});
            skLineSegment(sketch, "E44.27.1", {"start": v(129.93, 6.54) * mm, "end": v(124.5, 6.54) * mm});
            skLineSegment(sketch, "E44.27.2", {"start": v(124.5, 6.54) * mm, "end": v(124.5, 11.16) * mm});
            skLineSegment(sketch, "E44.27.3", {"start": v(124.5, 11.16) * mm, "end": v(129.93, 11.16) * mm});
            skLineSegment(sketch, "E44.28.0", {"start": v(124.5, 5.33) * mm, "end": v(129.85, 5.33) * mm});
            skLineSegment(sketch, "E44.28.1", {"start": v(129.85, 5.33) * mm, "end": v(129.85, 1.79) * mm});
            skLineSegment(sketch, "E44.28.2", {"start": v(129.85, 1.79) * mm, "end": v(124.5, 1.79) * mm});
            skLineSegment(sketch, "E44.28.3", {"start": v(124.5, 1.79) * mm, "end": v(124.5, 5.33) * mm});
            skSolve(sketch);
        }
        {
            var Q0;
            Q0 = qSketchRegion(id + "F14", true);
            extrude(context, id + "F15", {"entities" : qUnion([Q0]), "operationType" : NewBodyOperationType.REMOVE, "oppositeDirection" : true, "depth" : 0.5 * mm, "offsetDistance" : 25 * mm});
        }
    });
